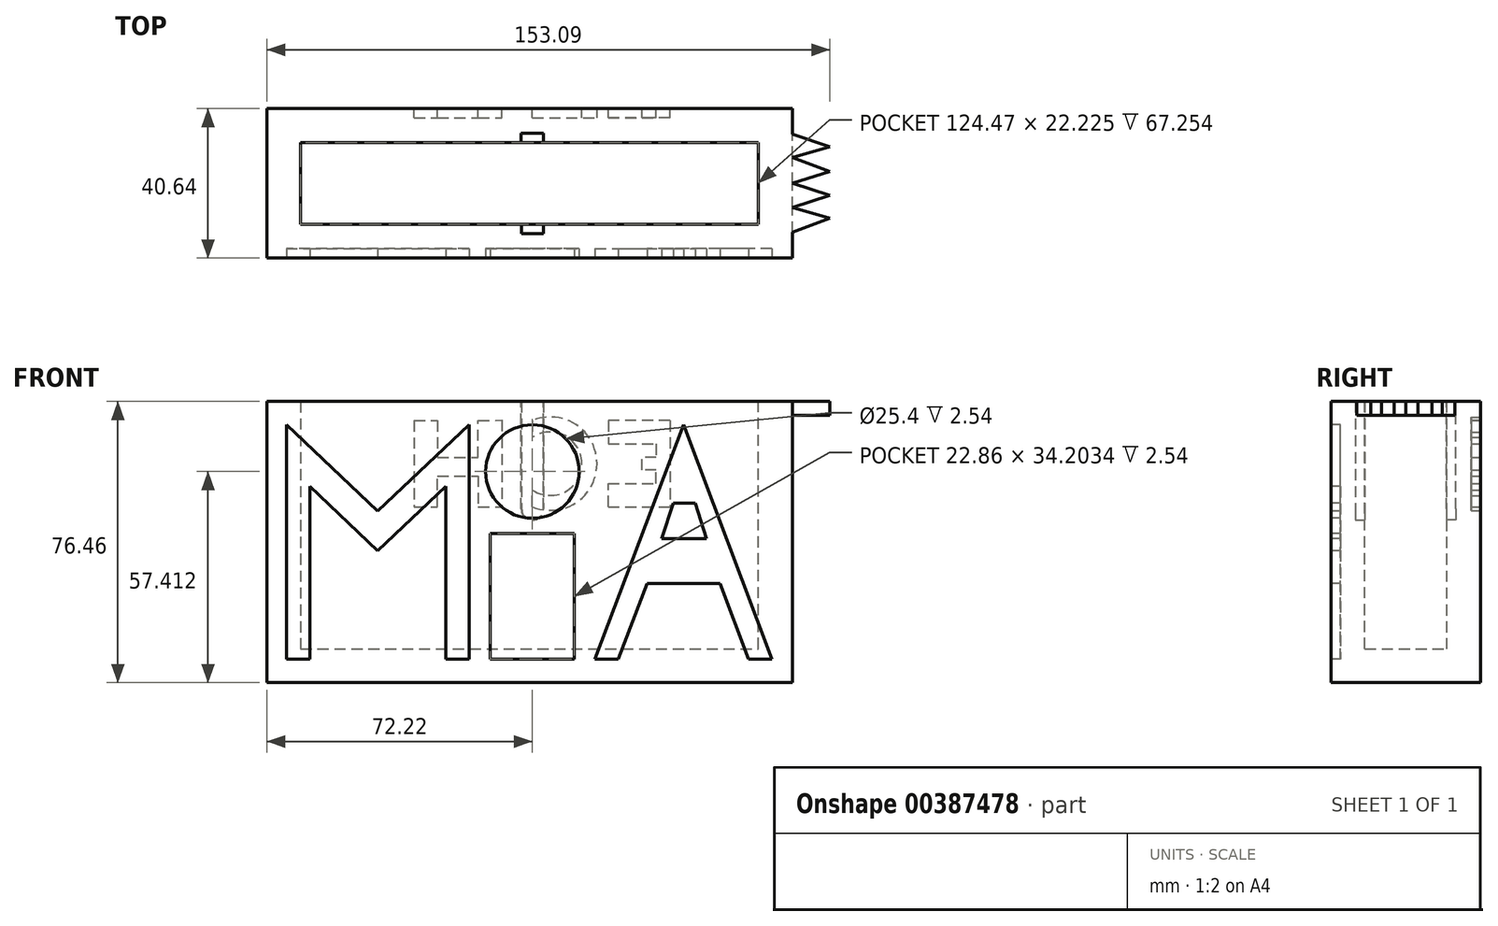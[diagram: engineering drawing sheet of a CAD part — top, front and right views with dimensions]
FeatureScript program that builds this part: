
annotation { "Feature Type Name" : "Feature", "Feature Type Description" : "" }
export const myFeature = defineFeature(function(context is Context, id is Id, definition is map)
    precondition{}
    {
        {
            var Q0;
            Q0=qCreatedBy(makeId("Front.planeOp"),FACE);
            var sketch = newSketch(context, id + "F0", { "sketchPlane" : qUnion([Q0])});
            skLineSegment(sketch, "E0", {"start": v(70.67, 49.47) * mm, "end": v(-72.22, 49.47) * mm});
            skLineSegment(sketch, "E1", {"start": v(-72.22, 49.47) * mm, "end": v(-72.22, -26.99) * mm});
            skLineSegment(sketch, "E2", {"start": v(-72.22, -26.99) * mm, "end": v(70.67, -26.99) * mm});
            skLineSegment(sketch, "E3", {"start": v(70.67, -26.99) * mm, "end": v(70.67, 49.47) * mm});
            skLineSegment(sketch, "E4", {"start": v(-72.22, 49.47) * mm, "end": v(-65.87, 49.47) * mm});
            skLineSegment(sketch, "E5", {"start": v(70.67, 49.47) * mm, "end": v(64.31, 49.47) * mm});
            skPoint(sketch, "E6", {"position": v(-65.87, 49.47) * mm});
            skPoint(sketch, "E7", {"position": v(64.31, 49.47) * mm});
            skSolve(sketch);
        }
        {
            var Q0;
            Q0 = qSketchRegion(id + "F0", true);
            extrude(context, id + "F1", {"entities" : qUnion([Q0]), "depth" : 40.64 * mm});
        }
        {
            var Q0;
            Q0=makeQuery(id+"F1.opExtrude","SWEPT_FACE",FACE,{"disambiguationData":[OSD([sQuery(id+"F0.wireOp",EDGE,"E0")])]});
            shell(context, id + "F2", {"entities" : qUnion([Q0]), "thickness" : 9.2 * mm});
        }
        {
            var Q0;
            {var subQ0=sQuery(id+"F0.wireOp",EDGE,"E3");var subQ1=sQuery(id+"F0.wireOp",EDGE,"E2");var subQ2=sQuery(id+"F0.wireOp",EDGE,"E1");var subQ3=sQuery(id+"F0.wireOp",EDGE,"E0");Q0=makeQuery(id+"F2.opShell","OFFSET_FACE",FACE,{"disambiguationData":[OSD([subQ3,subQ2,subQ1,subQ0]),TDD([makeQuery(id+"F1.opExtrude","CAP_FACE",FACE,{"disambiguationData":[OSD([subQ3,subQ2,subQ1,subQ0])],"isStart":true})])]});}
            var sketch = newSketch(context, id + "F3", { "sketchPlane" : qUnion([Q0])});
            skArc(sketch, "E8", {"start": v(-3.05, 20.26) * mm, "mid": v(0, 17.21) * mm, "end": v(3.05, 20.26) * mm});
            skLineSegment(sketch, "E9", {"start": v(3.05, 20.26) * mm, "end": v(3.05, 49.47) * mm});
            skLineSegment(sketch, "E10", {"start": v(-3.05, 20.26) * mm, "end": v(-3.05, 49.47) * mm});
            skSolve(sketch);
        }
        {
            var Q0;
            {var subQ0=sQuery(id+"F0.wireOp",EDGE,"E5");var subQ1=sQuery(id+"F0.wireOp",EDGE,"E4");var subQ2=sQuery(id+"F0.wireOp",EDGE,"E0");Q0=makeQuery(id+"FLhnWdOYaeVk9hF_1.boolean.opBoolean","MERGE",FACE,{"derivedFrom":[makeQuery(id+"FYobigN9pg2fOXs_2.boolean.opBoolean","MERGE",FACE,{"derivedFrom":[makeQuery(id+"F1.opExtrude","SWEPT_FACE",FACE,{"disambiguationData":[OSD([subQ2,subQ1,subQ0])]}),makeQuery(id+"FYobigN9pg2fOXs_2.opThicken","SWEPT_FACE",FACE,{"disambiguationData":[OSD([subQ2,subQ1,subQ0])]})]}),makeQuery(id+"FLhnWdOYaeVk9hF_1.opThicken","SWEPT_FACE",FACE,{"disambiguationData":[OSD([subQ2,subQ1,subQ0])]})]});}
            var sketch = newSketch(context, id + "F4", { "sketchPlane" : qUnion([Q0])});
            skLineSegment(sketch, "E11", {"start": v(70.67, -7) * mm, "end": v(80.87, -10.4) * mm});
            skLineSegment(sketch, "E12", {"start": v(80.87, -23.52) * mm, "end": v(70.67, -20.32) * mm});
            skLineSegment(sketch, "E13", {"start": v(70.67, -20.32) * mm, "end": v(80.87, -17.04) * mm});
            skLineSegment(sketch, "E14", {"start": v(80.87, -17.04) * mm, "end": v(70.67, -13.26) * mm});
            skLineSegment(sketch, "E15", {"start": v(70.67, -13.26) * mm, "end": v(80.87, -10.4) * mm});
            skLineSegment(sketch, "E16", {"start": v(80.87, -23.52) * mm, "end": v(70.67, -26.9) * mm});
            skLineSegment(sketch, "E17", {"start": v(70.67, -26.9) * mm, "end": v(80.87, -29.83) * mm});
            skLineSegment(sketch, "E18", {"start": v(70.67, -33.66) * mm, "end": v(80.87, -29.83) * mm});
            skSolve(sketch);
        }
        {
            var Q0;
            Q0=makeQuery(id+"F3.imprint","IMPRINT",FACE,{"disambiguationData":[TD([[makeQuery(id+"F3.imprint","IMPRINT",EDGE,{"derivedFrom":sQuery(id+"F3.wireOp",EDGE,"E8")}),1.0]])]});
            extrude(context, id + "F5", {"entities" : qUnion([Q0]), "operationType" : NewBodyOperationType.REMOVE, "oppositeDirection" : true, "depth" : 2.54 * mm});
        }
        {
            var Q0;
            {var subQ0=sQuery(id+"F0.wireOp",EDGE,"E5");var subQ1=sQuery(id+"F0.wireOp",EDGE,"E4");var subQ2=sQuery(id+"F0.wireOp",EDGE,"E3");var subQ3=sQuery(id+"F0.wireOp",EDGE,"E2");var subQ4=sQuery(id+"F0.wireOp",EDGE,"E1");var subQ5=sQuery(id+"F0.wireOp",EDGE,"E0");Q0=makeQuery(id+"F2.opShell","OFFSET_FACE",FACE,{"disambiguationData":[OSD([subQ5,subQ4,subQ3,subQ2,subQ1,subQ0]),TDD([makeQuery(id+"F1.opExtrude","CAP_FACE",FACE,{"disambiguationData":[OSD([subQ5,subQ4,subQ3,subQ2,subQ1,subQ0])],"isStart":false})])]});}
            var sketch = newSketch(context, id + "F6", { "sketchPlane" : qUnion([Q0])});
            skLineSegment(sketch, "E19", {"start": v(0, 49.47) * mm, "end": v(2.93, 49.47) * mm});
            skLineSegment(sketch, "E20", {"start": v(0, 49.47) * mm, "end": v(-3.04, 49.47) * mm});
            skLineSegment(sketch, "E21", {"start": v(-3.04, 49.47) * mm, "end": v(-3.04, 20.26) * mm});
            skLineSegment(sketch, "E22", {"start": v(2.93, 49.47) * mm, "end": v(2.93, 20.26) * mm});
            skArc(sketch, "E23", {"start": v(-3.04, 20.26) * mm, "mid": v(-0.06, 17.28) * mm, "end": v(2.93, 20.26) * mm});
            skSolve(sketch);
        }
        {
            var Q0;
            Q0 = qSketchRegion(id + "F6", true);
            extrude(context, id + "F7", {"entities" : qUnion([Q0]), "operationType" : NewBodyOperationType.REMOVE, "oppositeDirection" : true, "depth" : 2.54 * mm});
        }
        {
            var Q0;
            {var subQ0=sQuery(id+"F4.wireOp",EDGE,"E11");Q0=makeQuery(id+"F4.imprint","IMPRINT",FACE,{"disambiguationData":[TD([[makeQuery(id+"F4.imprint","IMPRINT",EDGE,{"derivedFrom":subQ0}),-1.0]])]});}
            var Q1;
            {var subQ0=sQuery(id+"F4.wireOp",EDGE,"E13");Q1=makeQuery(id+"F4.imprint","IMPRINT",FACE,{"disambiguationData":[TD([[makeQuery(id+"F4.imprint","IMPRINT",EDGE,{"derivedFrom":subQ0}),1.0]])]});}
            var Q2;
            {var subQ0=sQuery(id+"F4.wireOp",EDGE,"E12");Q2=makeQuery(id+"F4.imprint","IMPRINT",FACE,{"disambiguationData":[TD([[makeQuery(id+"F4.imprint","IMPRINT",EDGE,{"derivedFrom":subQ0}),1.0]])]});}
            var Q3;
            {var subQ0=sQuery(id+"F4.wireOp",EDGE,"E17");Q3=makeQuery(id+"F4.imprint","IMPRINT",FACE,{"disambiguationData":[TD([[makeQuery(id+"F4.imprint","IMPRINT",EDGE,{"derivedFrom":subQ0}),-1.0]])]});}
            extrude(context, id + "F8", {"entities" : qUnion([Q0, Q1, Q2, Q3]), "operationType" : NewBodyOperationType.ADD, "oppositeDirection" : true, "depth" : 3.8 * mm});
        }
        {
            var Q0;
            Q0=makeQuery(id+"F1.opExtrude","CAP_FACE",FACE,{"disambiguationData":[OSD([sQuery(id+"F0.wireOp",EDGE,"E0"),sQuery(id+"F0.wireOp",EDGE,"E1"),sQuery(id+"F0.wireOp",EDGE,"E2"),sQuery(id+"F0.wireOp",EDGE,"E3"),sQuery(id+"F0.wireOp",EDGE,"E4"),sQuery(id+"F0.wireOp",EDGE,"E5")])],"isStart":false});
            var sketch = newSketch(context, id + "F9", { "sketchPlane" : qUnion([Q0])});
            skLineSegment(sketch, "E24", {"start": v(-66.9, -20.64) * mm, "end": v(-60.55, -20.64) * mm});
            skCircle(sketch, "E25", {"center": v(0, 30.42) * mm, "radius": 12.7 * mm});
            skLineSegment(sketch, "E26", {"start": v(-11.43, 13.56) * mm, "end": v(-11.43, -20.64) * mm});
            skLineSegment(sketch, "E27", {"start": v(-11.43, -20.64) * mm, "end": v(11.43, -20.64) * mm});
            skLineSegment(sketch, "E28", {"start": v(11.43, 13.56) * mm, "end": v(11.43, -20.64) * mm});
            skLineSegment(sketch, "E29.trimOffspring", {"start": v(17.02, -20.64) * mm, "end": v(23.37, -20.64) * mm});
            skLineSegment(sketch, "E30", {"start": v(11.43, 13.56) * mm, "end": v(-11.43, 13.56) * mm});
            skLineSegment(sketch, "E31", {"start": v(-17.21, -20.64) * mm, "end": v(-17.21, 43.12) * mm});
            skLineSegment(sketch, "E32", {"start": v(-66.9, -20.64) * mm, "end": v(-66.9, 43.12) * mm});
            skLineSegment(sketch, "E33", {"start": v(-42.06, 19.63) * mm, "end": v(-17.21, 43.12) * mm});
            skLineSegment(sketch, "E34", {"start": v(-42.06, 19.63) * mm, "end": v(-66.9, 43.12) * mm});
            skLineSegment(sketch, "E35", {"start": v(-60.55, -20.64) * mm, "end": v(-60.55, 26.35) * mm});
            skLineSegment(sketch, "E36", {"start": v(-60.55, 26.35) * mm, "end": v(-42.06, 8.86) * mm});
            skLineSegment(sketch, "E37", {"start": v(-17.21, -20.64) * mm, "end": v(-23.56, -20.64) * mm});
            skLineSegment(sketch, "E38", {"start": v(-23.56, -20.64) * mm, "end": v(-23.56, 26.35) * mm});
            skLineSegment(sketch, "E39", {"start": v(-23.56, 26.35) * mm, "end": v(-42.06, 8.86) * mm});
            skLineSegment(sketch, "E40.trimOffspring", {"start": v(-23.56, -20.64) * mm, "end": v(-17.21, -20.64) * mm});
            skPoint(sketch, "E41", {"position": v(17.02, -20.64) * mm});
            skPoint(sketch, "E42", {"position": v(65.08, -20.64) * mm});
            skPoint(sketch, "E43", {"position": v(41.05, 43.12) * mm});
            skLineSegment(sketch, "E44", {"start": v(17.02, -20.64) * mm, "end": v(41.05, 43.12) * mm});
            skLineSegment(sketch, "E45", {"start": v(65.08, -20.64) * mm, "end": v(41.05, 43.12) * mm});
            skLineSegment(sketch, "E46", {"start": v(65.08, -20.64) * mm, "end": v(58.73, -20.64) * mm});
            skLineSegment(sketch, "E47", {"start": v(58.73, -20.64) * mm, "end": v(50.98, 0) * mm});
            skLineSegment(sketch, "E48", {"start": v(23.37, -20.64) * mm, "end": v(31.14, 0) * mm});
            skLineSegment(sketch, "E49.trimOffspring", {"start": v(58.73, -20.64) * mm, "end": v(65.08, -20.64) * mm});
            skLineSegment(sketch, "E50", {"start": v(50.98, 0) * mm, "end": v(31.14, 0) * mm});
            skPoint(sketch, "E51.endSnap0", {"position": v(-29.63, 31.37) * mm});
            skLineSegment(sketch, "E52", {"start": v(47.27, 12.18) * mm, "end": v(35.14, 12.18) * mm});
            skLineSegment(sketch, "E53", {"start": v(38.32, 21.9) * mm, "end": v(44.32, 21.9) * mm});
            skLineSegment(sketch, "E54", {"start": v(47.27, 12.18) * mm, "end": v(44.32, 21.9) * mm});
            skLineSegment(sketch, "E55", {"start": v(38.32, 21.9) * mm, "end": v(35.14, 12.18) * mm});
            skSolve(sketch);
        }
        {
            var Q0;
            Q0=makeQuery(id+"F9.imprint","IMPRINT",FACE,{"disambiguationData":[TD([[makeQuery(id+"F9.imprint","IMPRINT",EDGE,{"derivedFrom":sQuery(id+"F9.wireOp",EDGE,"E31")}),1.0]])]});
            var Q1;
            Q1=makeQuery(id+"F9.imprint","IMPRINT",FACE,{"disambiguationData":[TD([[makeQuery(id+"F9.imprint","IMPRINT",EDGE,{"derivedFrom":sQuery(id+"F9.wireOp",EDGE,"E25")}),1.0]])]});
            var Q2;
            Q2=makeQuery(id+"F9.imprint","IMPRINT",FACE,{"disambiguationData":[TD([[makeQuery(id+"F9.imprint","IMPRINT",EDGE,{"derivedFrom":sQuery(id+"F9.wireOp",EDGE,"E26")}),1.0]])]});
            var Q3;
            Q3=makeQuery(id+"F9.imprint","IMPRINT",FACE,{"disambiguationData":[TD([[makeQuery(id+"F9.imprint","IMPRINT",EDGE,{"derivedFrom":sQuery(id+"F9.wireOp",EDGE,"E44")}),-1.0]])]});
            extrude(context, id + "F10", {"entities" : qUnion([Q0, Q1, Q2, Q3]), "operationType" : NewBodyOperationType.REMOVE, "oppositeDirection" : true, "depth" : 2.54 * mm});
        }
        {
            var Q0;
            Q0=makeQuery(id+"F1.opExtrude","CAP_FACE",FACE,{"disambiguationData":[OSD([sQuery(id+"F0.wireOp",EDGE,"E0"),sQuery(id+"F0.wireOp",EDGE,"E1"),sQuery(id+"F0.wireOp",EDGE,"E2"),sQuery(id+"F0.wireOp",EDGE,"E3"),sQuery(id+"F0.wireOp",EDGE,"E4"),sQuery(id+"F0.wireOp",EDGE,"E5")])],"isStart":true});
            var sketch = newSketch(context, id + "F11", { "sketchPlane" : qUnion([Q0])});
            skLineSegment(sketch, "E56", {"start": v(-43.93, 44.3) * mm, "end": v(-64.28, 44.3) * mm});
            skLineSegment(sketch, "E57", {"start": v(-64.28, 44.3) * mm, "end": v(-43.93, 44.3) * mm});
            skLineSegment(sketch, "E58", {"start": v(-43.93, 44.3) * mm, "end": v(-43.93, 38.14) * mm});
            skLineSegment(sketch, "E59", {"start": v(-64.28, 44.3) * mm, "end": v(-64.28, 38.14) * mm});
            skLineSegment(sketch, "E60", {"start": v(-64.28, 38.14) * mm, "end": v(-57.8, 38.14) * mm});
            skLineSegment(sketch, "E61", {"start": v(-51.33, 38.14) * mm, "end": v(-51.33, 20.83) * mm});
            skLineSegment(sketch, "E62", {"start": v(-51.33, 20.83) * mm, "end": v(-57.8, 20.83) * mm});
            skLineSegment(sketch, "E63", {"start": v(-57.8, 20.83) * mm, "end": v(-57.8, 38.14) * mm});
            skLineSegment(sketch, "E64.trimOffspring", {"start": v(-51.33, 38.14) * mm, "end": v(-43.93, 38.14) * mm});
            skLineSegment(sketch, "E65", {"start": v(-37.39, 44.3) * mm, "end": v(-37.39, 20.83) * mm});
            skLineSegment(sketch, "E66", {"start": v(-37.39, 44.3) * mm, "end": v(-20.62, 44.3) * mm});
            skLineSegment(sketch, "E67", {"start": v(-20.62, 20.83) * mm, "end": v(-37.39, 20.83) * mm});
            skLineSegment(sketch, "E68", {"start": v(-20.62, 44.3) * mm, "end": v(-20.62, 37.91) * mm});
            skLineSegment(sketch, "E69", {"start": v(-20.62, 20.83) * mm, "end": v(-20.62, 27.18) * mm});
            skLineSegment(sketch, "E70", {"start": v(-20.62, 27.18) * mm, "end": v(-33.62, 27.18) * mm});
            skLineSegment(sketch, "E71", {"start": v(-20.62, 37.91) * mm, "end": v(-33.62, 37.91) * mm});
            skLineSegment(sketch, "E72", {"start": v(-29.77, 30.81) * mm, "end": v(-29.77, 34.3) * mm});
            skLineSegment(sketch, "E73", {"start": v(-33.62, 37.91) * mm, "end": v(-33.62, 34.3) * mm});
            skLineSegment(sketch, "E74", {"start": v(-33.62, 27.18) * mm, "end": v(-33.62, 30.81) * mm});
            skLineSegment(sketch, "E75", {"start": v(-33.62, 34.3) * mm, "end": v(-29.77, 34.3) * mm});
            skLineSegment(sketch, "E76", {"start": v(-33.62, 30.81) * mm, "end": v(-29.77, 30.81) * mm});
            skArc(sketch, "E77", {"start": v(0, 44.3) * mm, "mid": v(-17.55, 32.57) * mm, "end": v(0, 20.83) * mm});
            skLineSegment(sketch, "E78", {"start": v(0, 44.3) * mm, "end": v(0, 39.73) * mm});
            skLineSegment(sketch, "E79", {"start": v(0, 20.83) * mm, "end": v(0, 25.4) * mm});
            skArc(sketch, "E80", {"start": v(0, 39.73) * mm, "mid": v(-13.45, 32.57) * mm, "end": v(0, 25.4) * mm});
            skLineSegment(sketch, "E81", {"start": v(25.81, 20.83) * mm, "end": v(25.81, 29.25) * mm});
            skLineSegment(sketch, "E82", {"start": v(25.81, 29.25) * mm, "end": v(14.72, 29.25) * mm});
            skLineSegment(sketch, "E83", {"start": v(14.72, 29.25) * mm, "end": v(14.72, 20.83) * mm});
            skLineSegment(sketch, "E84", {"start": v(25.81, 44.3) * mm, "end": v(25.81, 34.24) * mm});
            skLineSegment(sketch, "E85", {"start": v(25.81, 34.24) * mm, "end": v(14.72, 34.24) * mm});
            skLineSegment(sketch, "E86", {"start": v(14.72, 34.24) * mm, "end": v(14.72, 44.3) * mm});
            skLineSegment(sketch, "E87", {"start": v(8.37, 44.4) * mm, "end": v(8.37, 20.83) * mm});
            skLineSegment(sketch, "E88", {"start": v(32.16, 44.27) * mm, "end": v(32.16, 20.83) * mm});
            skLineSegment(sketch, "E89", {"start": v(14.72, 20.83) * mm, "end": v(8.37, 20.83) * mm});
            skLineSegment(sketch, "E90", {"start": v(14.72, 44.3) * mm, "end": v(8.37, 44.4) * mm});
            skLineSegment(sketch, "E91", {"start": v(32.16, 44.27) * mm, "end": v(25.81, 44.3) * mm});
            skLineSegment(sketch, "E92", {"start": v(32.16, 20.83) * mm, "end": v(25.81, 20.83) * mm});
            skSolve(sketch);
        }
        {
            var Q0;
            Q0=makeQuery(id+"F11.imprint","IMPRINT",FACE,{"disambiguationData":[TD([[makeQuery(id+"F11.imprint","IMPRINT",EDGE,{"derivedFrom":sQuery(id+"F11.wireOp",EDGE,"E57")}),-1.0]])]});
            var Q1;
            Q1=makeQuery(id+"F11.imprint","IMPRINT",FACE,{"disambiguationData":[TD([[makeQuery(id+"F11.imprint","IMPRINT",EDGE,{"derivedFrom":sQuery(id+"F11.wireOp",EDGE,"E65")}),1.0]])]});
            var Q2;
            Q2=makeQuery(id+"F11.imprint","IMPRINT",FACE,{"disambiguationData":[TD([[makeQuery(id+"F11.imprint","IMPRINT",EDGE,{"derivedFrom":sQuery(id+"F11.wireOp",EDGE,"E77")}),1.0]])]});
            var Q3;
            Q3=makeQuery(id+"F11.imprint","IMPRINT",FACE,{"disambiguationData":[TD([[makeQuery(id+"F11.imprint","IMPRINT",EDGE,{"derivedFrom":sQuery(id+"F11.wireOp",EDGE,"E81")}),-1.0]])]});
            extrude(context, id + "F12", {"entities" : qUnion([Q0, Q1, Q2, Q3]), "operationType" : NewBodyOperationType.REMOVE, "oppositeDirection" : true, "depth" : 2.54 * mm});
        }
    });
